# Revit family: bimlib_narujnyeblokisistemakondicionirovaniya_mrv-s-l_5-7hp_haier
name_source: partatom
category: Оборудование
units: mm (PartAtom-declared; Revit-internal decimal feet)

## family parameters
Всегда вертикально = Да
На основе рабочей плоскости = Нет
Общий = Нет
При загрузке вырезать с полостями = Нет
Размер круглого соединителя = Использовать диаметр
Тип детали = Нормальный
Точка расчета площади = Нет

## types (3) — shared parameters
ADSK_URL документации изделия = https://haierproff.ru
ADSK_URL страницы изделия = https://haierproff.ru
ADSK_Версия Revit = 2017
ADSK_Группирование = VRF-системы MRV-S'
ADSK_Единица измерения = шт.
ADSK_Завод-изготовитель = Haier Group
ADSK_Классификация нагрузок = ОВК
ADSK_Количество = 1
ADSK_Коэффициент мощности = 1
ADSK_Обозначение = MRV-S'
ADSK_Размер_Глубина = 370 мм
ADSK_Размер_Ширина = 950 мм
ADSK_Расход воздуха = 7200.0 м³/ч
BL_BIM library = https://bimlib.pro
HG_URL поставщика = www.haierproff.ru
URL = www.haier.com
Диаметр_Жидкость = 9.52 мм
Заправка хладагента = 4.00 кг
Изготовитель = Haier Group
Производитель компрессора = MITSUBISHI ELECTRIC
Работа на обогрев = Нет
Рабочий диапазон_Обогрев = -20 ~ 27
Рабочий диапазон_Охлаждение = -5 ~ 50
Сбоку = Подключение : Сбоку
Сзади = Подключение : Сзади
Снизу = Подключение : Снизу
Спереди = Подключение : Спереди
Тип компрессора = Роторный
Тип хладагента = R410A
Частота тока = 50 Гц
zero-valued in all types: Отметка по умолчанию

## per-type parameters (varying)
| type | ADSK_Код изделия | ADSK_Количество фаз | ADSK_Масса | ADSK_Наименование | ADSK_Наименование краткое | ADSK_Напряжение | ADSK_Номинальная мощность | ADSK_Полная мощность | ADSK_Размер_Высота | Диаметр_Газ | Звуковое давление | Обогрев_Потребляемая мощность | Охлаждение_Потребляемая мощность | Теплопроизводительность | Холодопроизводительность |
| AU07NFPEUA_7HP_HAIER | AU07NFPEUA | 3 | 115 | Наружный блок VRF-системы кондиционирования MRV-S', 7HP | VRF-системы MRV-S', 7HP | 400 В | 4750 Вт | 4750 В·А | 1340 мм | 15.88 мм | 54 | 5 кВт | 5 кВт | 20 кВт | 18 кВт |
| AU052FPEUA_5HP_HAIER | AU052FPEUA | 1 | 108 | Наружный блок VRF-системы кондиционирования MRV-S', 5HP | VRF-системы MRV-S', 5HP | 230 В | 3700 Вт | 3700 В·А | 1348 мм | 15.88 мм | 52 | 4 кВт | 4 кВт | 16 кВт | 14 кВт |
| AU072FPEUA_7HP_HAIER | AU072FPEUA | 1 | 108 | Наружный блок VRF-системы кондиционирования MRV-S', 7HP | VRF-системы MRV-S', 7HP | 230 В | 4750 Вт | 4750 В·А | 1348 мм | 19.05 мм | 54 | 5 кВт | 5 кВт | 20 кВт | 18 кВт |
